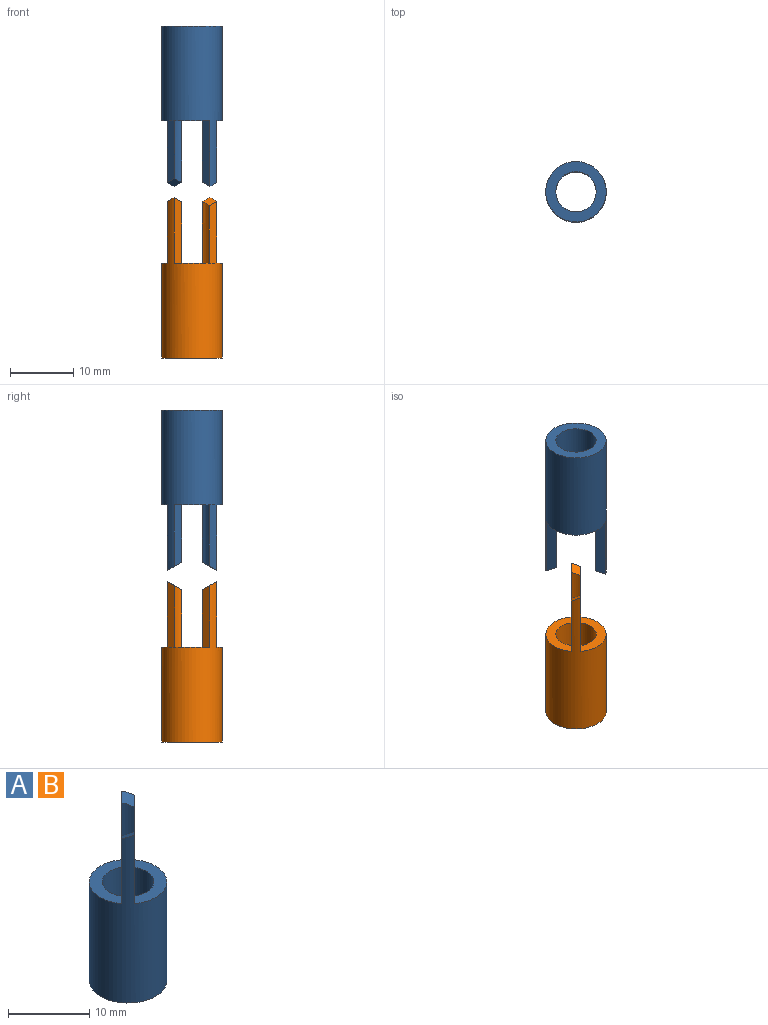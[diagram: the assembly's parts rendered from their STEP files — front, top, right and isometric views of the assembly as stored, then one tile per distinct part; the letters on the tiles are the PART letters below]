
ASSEMBLY  parts=2 mates=1
PART A: 11 faces, bbox 9.5x9.5x25.3 mm
  f0: cylinder r=4.76mm len=25.28mm, axis (0,0,-1), area 477.4mm2, adj f2,f3,f4,f5,f6,f7,f8,f9
  f1: cylinder r=3.17mm len=24.62mm, axis (0,0,-1), area 326.7mm2, adj f2,f3,f4,f5,f6,f7,f8,f9
  f2: plane 2.22x2.22mm, normal (0,0.5,0.87), area 2.8mm2, adj f0,f1,f6,f9
  f3: plane 2.22x2.22mm, normal (0,-0.5,0.87), area 2.8mm2, adj f0,f1,f7,f10
  f4: plane 9.53x9.53mm, normal (0,0,-1), area 39.6mm2, adj f0,f1
  f5: plane 7.55x7.55mm, normal (0,0,1), area 17.4mm2, adj f0,f1,f6,f7
  f6: plane 9.74x1.14mm, normal (-0.71,0.71,0), area 15.2mm2, adj f0,f1,f2,f5
  f7: plane 10.36x1.14mm, normal (-0.71,0.71,0), area 16.2mm2, adj f0,f1,f3,f5
  f8: plane 7.55x7.55mm, normal (0,0,1), area 17.4mm2, adj f0,f1,f9,f10
  f9: plane 10.36x1.14mm, normal (0.71,-0.71,0), area 16.2mm2, adj f0,f1,f2,f8
  f10: plane 9.74x1.14mm, normal (0.71,-0.71,0), area 15.2mm2, adj f0,f1,f3,f8
PART B: same geometry as A
PLACE A rot(axis=(1,0,0),180deg) t=(19.13,3.7,25)mm
PLACE B t=(19.13,3.7,-27.34)mm
MATE cylindrical A.f0 <-> B.f0  axis (0,0,1) through (19.13,3.7,12.28)mm
